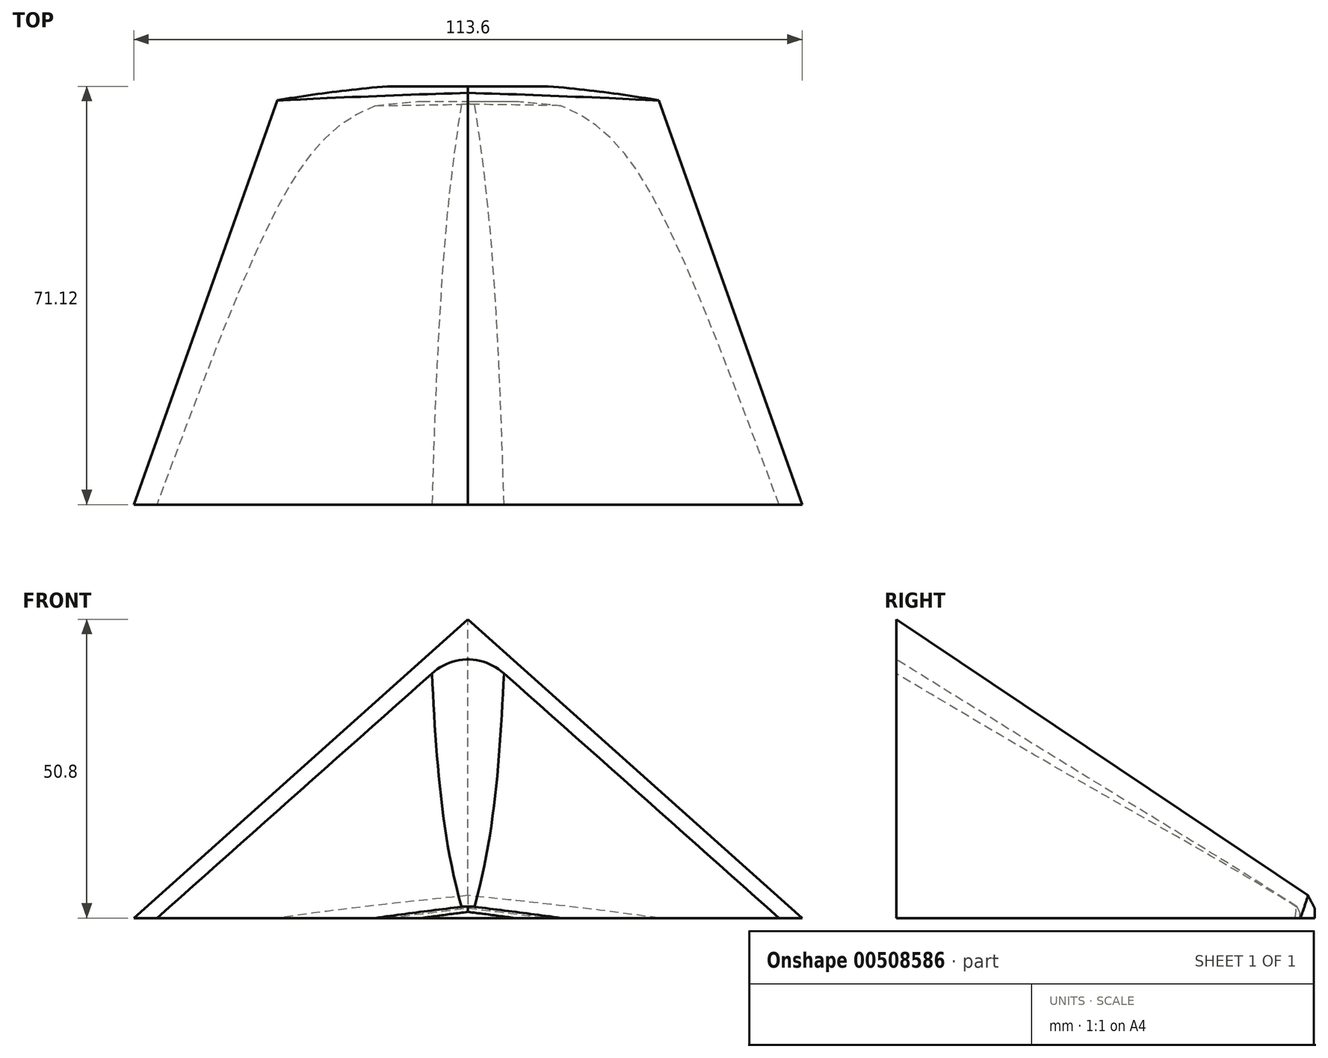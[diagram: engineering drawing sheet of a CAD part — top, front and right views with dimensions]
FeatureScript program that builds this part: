
annotation { "Feature Type Name" : "Feature", "Feature Type Description" : "" }
export const myFeature = defineFeature(function(context is Context, id is Id, definition is map)
    precondition{}
    {
        {
            var Q0;
            Q0=qCreatedBy(makeId("Front.planeOp"),FACE);
            var sketch = newSketch(context, id + "F0", { "sketchPlane" : qUnion([Q0])});
            skLineSegment(sketch, "E0", {"start": v(0, 0) * mm, "end": v(-56.8, 0) * mm});
            skLineSegment(sketch, "E1", {"start": v(-56.8, 0) * mm, "end": v(0, 50.8) * mm});
            skLineSegment(sketch, "E2", {"start": v(0, 50.8) * mm, "end": v(0, 0) * mm});
            skSolve(sketch);
        }
        {
            var Q0;
            Q0=qCreatedBy(makeId("Front.planeOp"),FACE);
            cPlane(context, id + "F1", {"entities" : qUnion([Q0]), "cplaneType" : CPlaneType.OFFSET, "offset" : 71.12 * mm, "oppositeDirection" : true, "width" : 152.4 * mm, "height" : 152.4 * mm});
        }
        {
            var Q0;
            Q0=qCreatedBy(id+"F1.planeOp",FACE);
            var sketch = newSketch(context, id + "F2", { "sketchPlane" : qUnion([Q0])});
            skLineSegment(sketch, "E3", {"start": v(0, 3.06) * mm, "end": v(-31.58, 0) * mm});
            skLineSegment(sketch, "E4", {"start": v(-31.58, 0) * mm, "end": v(0, 0) * mm});
            skLineSegment(sketch, "E5", {"start": v(0, 0) * mm, "end": v(0, 3.06) * mm});
            skSolve(sketch);
        }
        {
            var Q0;
            Q0=makeQuery(id+"F2.imprint","IMPRINT",FACE,{"disambiguationData":[TD([[makeQuery(id+"F2.imprint","IMPRINT",EDGE,{"derivedFrom":sQuery(id+"F2.wireOp",EDGE,"E3")}),1.0]])]});
            var Q1;
            Q1=makeQuery(id+"F0.imprint","IMPRINT",FACE,{"disambiguationData":[TD([[makeQuery(id+"F0.imprint","IMPRINT",EDGE,{"derivedFrom":sQuery(id+"F0.wireOp",EDGE,"E0")}),-1.0]])]});
            loft(context, id + "F3", {"sheetProfilesArray" : [{ "sheetProfileEntities" : qUnion([Q0]) }, { "sheetProfileEntities" : qUnion([Q1]) }]});
        }
        {
            var Q0;
            Q0=makeQuery(id+"F3.opLoft","SWEPT_BODY",BODY,{"disambiguationData":[OSD([makeQuery(id+"F0.imprint","IMPRINT",FACE,{"disambiguationData":[TD([[makeQuery(id+"F0.imprint","IMPRINT",EDGE,{"derivedFrom":sQuery(id+"F0.wireOp",EDGE,"E0")}),-1.0]])]}),makeQuery(id+"F2.imprint","IMPRINT",FACE,{"disambiguationData":[TD([[makeQuery(id+"F2.imprint","IMPRINT",EDGE,{"derivedFrom":sQuery(id+"F2.wireOp",EDGE,"E3")}),1.0]])]})])]});
            var Q1;
            Q1=qCreatedBy(makeId("Right.planeOp"),FACE);
            mirror(context, id + "F4", {"operationType" : NewBodyOperationType.ADD, "entities" : qUnion([Q0]), "mirrorPlane" : qUnion([Q1])});
        }
        {
            var Q0;
            {var subQ0=sQuery(id+"F2.wireOp",EDGE,"E3");var subQ1=sQuery(id+"F2.wireOp",EDGE,"E4");var subQ2=sQuery(id+"F2.wireOp",EDGE,"E5");Q0=makeQuery(id+"F4.opPattern","COPY",EDGE,{"derivedFrom":makeQuery(id+"F3.opLoft","MID_CAP_EDGE",EDGE,{"disambiguationData":[OSD([subQ0,subQ1,subQ2]),TDD([makeQuery(id+"F2.imprint","INTERSECT",VERTEX,{"derivedFrom":[subQ0,subQ2]}),makeQuery(id+"F2.imprint","INTERSECT",VERTEX,{"derivedFrom":[subQ0,subQ1]}),makeQuery(id+"F2.imprint","IMPRINT",EDGE,{"derivedFrom":subQ0})])],"capPos":0.0}),"instanceName":"1"});}
            var Q1;
            {var subQ0=sQuery(id+"F2.wireOp",EDGE,"E3");var subQ1=sQuery(id+"F2.wireOp",EDGE,"E4");var subQ2=sQuery(id+"F2.wireOp",EDGE,"E5");Q1=makeQuery(id+"F3.opLoft","MID_CAP_EDGE",EDGE,{"disambiguationData":[OSD([subQ0,subQ1,subQ2]),TDD([makeQuery(id+"F2.imprint","INTERSECT",VERTEX,{"derivedFrom":[subQ0,subQ2]}),makeQuery(id+"F2.imprint","INTERSECT",VERTEX,{"derivedFrom":[subQ0,subQ1]}),makeQuery(id+"F2.imprint","IMPRINT",EDGE,{"derivedFrom":subQ0})])],"capPos":0.0});}
            chamfer(context, id + "F5", {"entities" : qUnion([Q0, Q1]), "width" : 2.54 * mm, "tangentPropagation" : true});
        }
        {
            var Q0;
            {var subQ0=makeQuery(id+"F3.opLoft","CAP_FACE",FACE,{"disambiguationData":[OSD([makeQuery(id+"F0.imprint","IMPRINT",FACE,{"disambiguationData":[TD([[makeQuery(id+"F0.imprint","IMPRINT",EDGE,{"derivedFrom":sQuery(id+"F0.wireOp",EDGE,"E0")}),-1.0]])]})])],"isStart":true});Q0=makeQuery(id+"F4.boolean.opBoolean","MERGE",FACE,{"derivedFrom":[subQ0,makeQuery(id+"F4.opPattern","COPY",FACE,{"derivedFrom":subQ0,"instanceName":"1"})]});}
            var Q1;
            {var subQ0=sQuery(id+"F2.wireOp",EDGE,"E4");var subQ1=sQuery(id+"F2.wireOp",EDGE,"E5");var subQ2=sQuery(id+"F2.wireOp",EDGE,"E3");var subQ3=sQuery(id+"F0.wireOp",EDGE,"E0");var subQ4=sQuery(id+"F0.wireOp",EDGE,"E1");var subQ5=sQuery(id+"F0.wireOp",EDGE,"E2");var subQ6=makeQuery(id+"F3.opLoft","SWEPT_FACE",FACE,{"disambiguationData":[OSD([subQ3,subQ4,subQ5,subQ2,subQ0,subQ1]),TDD([makeQuery(id+"F0.imprint","INTERSECT",VERTEX,{"derivedFrom":[subQ3,subQ5]}),makeQuery(id+"F0.imprint","INTERSECT",VERTEX,{"derivedFrom":[subQ3,subQ4]}),makeQuery(id+"F0.imprint","IMPRINT",EDGE,{"derivedFrom":subQ3}),makeQuery(id+"F2.imprint","INTERSECT",VERTEX,{"derivedFrom":[subQ2,subQ0]}),makeQuery(id+"F2.imprint","INTERSECT",VERTEX,{"derivedFrom":[subQ0,subQ1]}),makeQuery(id+"F2.imprint","IMPRINT",EDGE,{"derivedFrom":subQ0})])]});Q1=makeQuery(id+"F4.boolean.opBoolean","MERGE",FACE,{"derivedFrom":[subQ6,makeQuery(id+"F4.opPattern","COPY",FACE,{"derivedFrom":subQ6,"instanceName":"1"})]});}
            shell(context, id + "F6", {"entities" : qUnion([Q0, Q1]), "thickness" : 2.54 * mm});
        }
        {
            var Q0;
            Q0=makeQuery(id+"F6.opShell","OFFSET_EDGE",EDGE,{"disambiguationData":[OSD([sQuery(id+"F0.wireOp",EDGE,"E1"),sQuery(id+"F0.wireOp",EDGE,"E2"),sQuery(id+"F2.wireOp",EDGE,"E3"),sQuery(id+"F2.wireOp",EDGE,"E5")])]});
            fillet(context, id + "F7", {"entities" : qUnion([Q0]), "radius" : 10.16 * mm, "tangentPropagation" : true, "allowEdgeOverflow" : false});
        }
    });
